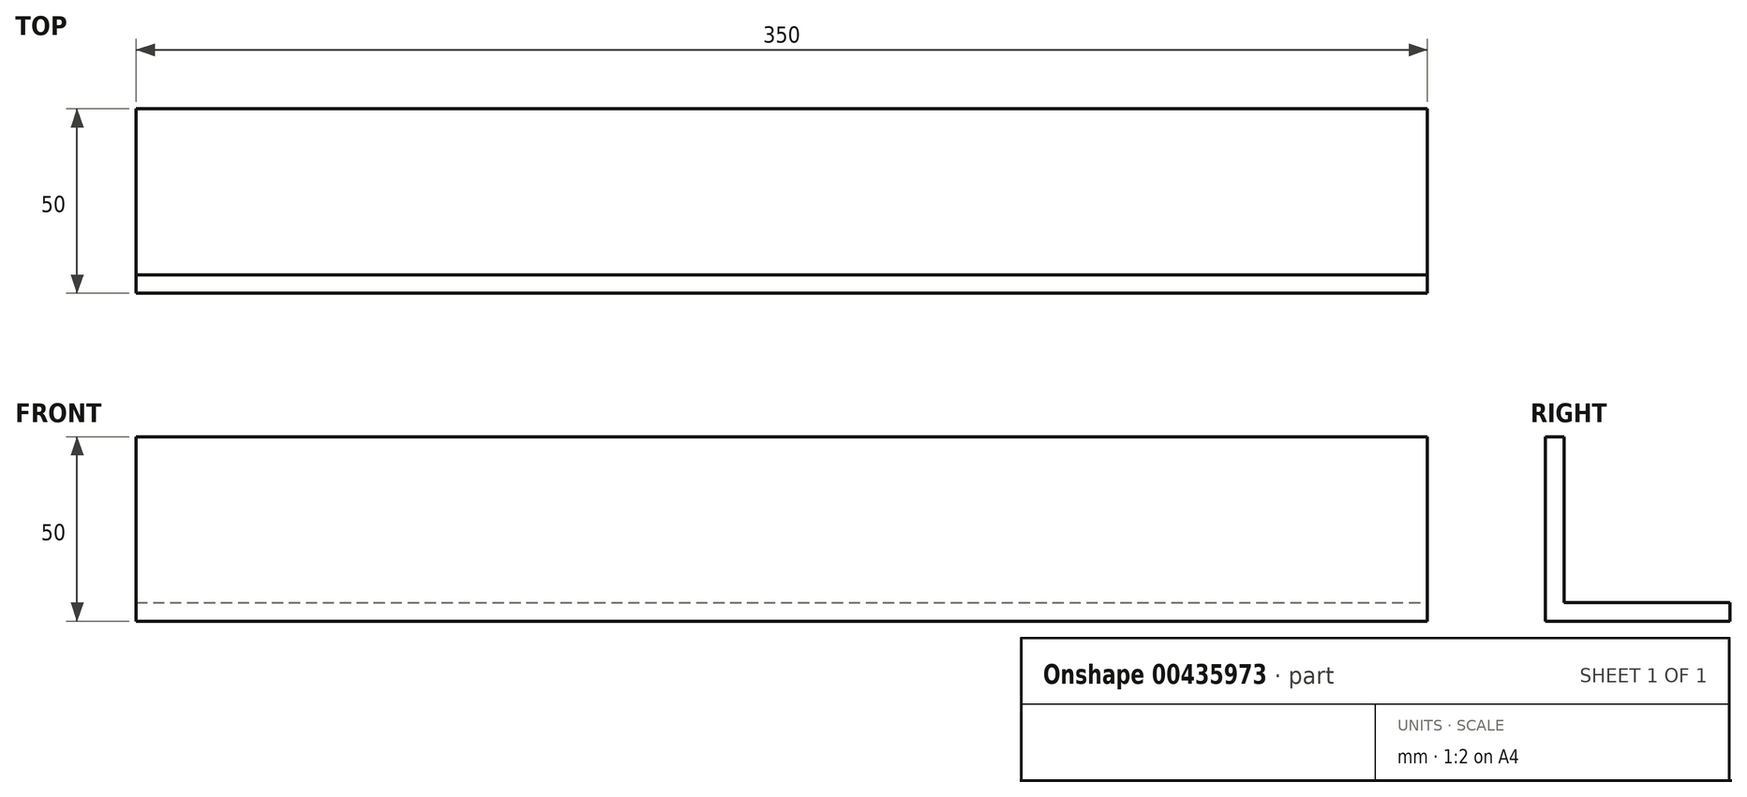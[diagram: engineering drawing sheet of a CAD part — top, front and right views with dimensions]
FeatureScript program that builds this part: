
annotation { "Feature Type Name" : "Feature", "Feature Type Description" : "" }
export const myFeature = defineFeature(function(context is Context, id is Id, definition is map)
    precondition{}
    {
        {
            var Q0;
            Q0=qCreatedBy(makeId("Right.planeOp"),FACE);
            var sketch = newSketch(context, id + "F0", { "sketchPlane" : qUnion([Q0])});
            skLineSegment(sketch, "E0.bottom", {"start": v(0, 0) * mm, "end": v(-50, 0) * mm});
            skLineSegment(sketch, "E0.right", {"start": v(-50, 0) * mm, "end": v(-50, 50) * mm});
            skLineSegment(sketch, "E1.0", {"start": v(0, 5) * mm, "end": v(-45, 5) * mm});
            skLineSegment(sketch, "E2.0", {"start": v(-45, 5) * mm, "end": v(-45, 50) * mm});
            skLineSegment(sketch, "E3", {"start": v(-50, 50) * mm, "end": v(-45, 50) * mm});
            skLineSegment(sketch, "E4", {"start": v(0, 5) * mm, "end": v(0, 0) * mm});
            skSolve(sketch);
        }
        {
            var Q0;
            Q0=qSketchRegion(id+"F0",true);
            extrude(context, id + "F1", {"entities" : qUnion([Q0]), "oppositeDirection" : true, "depth" : 350 * mm});
        }
    });
